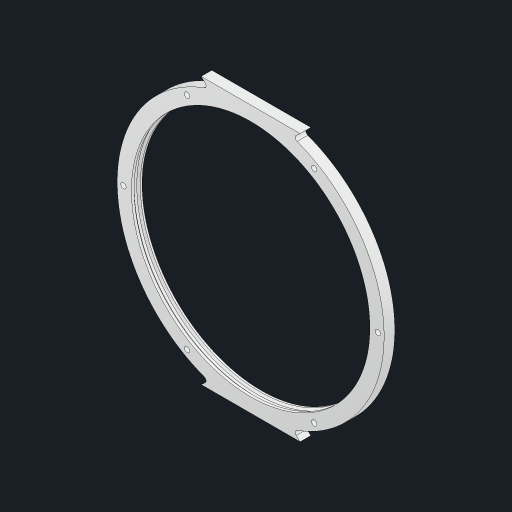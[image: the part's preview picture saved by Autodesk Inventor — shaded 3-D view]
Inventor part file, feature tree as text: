
AUTODESK INVENTOR PART (.ipt)
format: ipt  version: 2023.2 (Build 272271030, 271C)  size: 186,880 bytes
history: native  units: mm
features: sketch x4, extrude x4, mirror x2, revolve x1, fillet x1, pattern_circular x1
ambient origin geometry x8: Origin, YZ Plane, XZ Plane, XY Plane, X Axis, Y Axis, Z Axis, Center Point
bodies: Solid1 (feature_tree)
feature tree (13):
  sketch  "Sketch1"  dims[d0=134.0mm d1=150.0mm]
  extrude  "Extrusion1"  Depth=150.0mm
  extrude  "Extrusion2"  Depth=1.6mm
  mirror  "Mirror1"
  mirror  "Mirror2"
  revolve  "Revolution1"  [1 undecoded]
  extrude  "Extrusion3"  Depth=6.0mm
  extrude  "Extrusion4"  Depth=6.0mm TaperAngle=0.0deg
  fillet  "Fillet1"  Radius=5.0mm
  pattern_circular  "Circular Pattern1"  [2 undecoded]
  sketch  "Sketch2"  dims[d2=5.0mm d3=1.6mm]
  sketch  "Sketch3"  dims[d4=20.0mm d6=360.0deg d8=6.0mm d9=0.0mm]
  sketch  "Sketch4"  dims[d10=6.0mm d11=0.0mm d12=3.0mm d15=5.0mm d16=0.0mm d17=5.0mm d18=0.0mm d19=4.0mm d20=60.0mm d21=360.0deg d24=6.0mm d25=2.5mm d27=1.0mm d28=0.5mm d29=0.5mm d30=90.0deg]
note: 3 required parameter values undecoded (feature->parameter linkage not recoverable at this tier; creation-order binding heuristic only, values carry confidence <= 0.55)